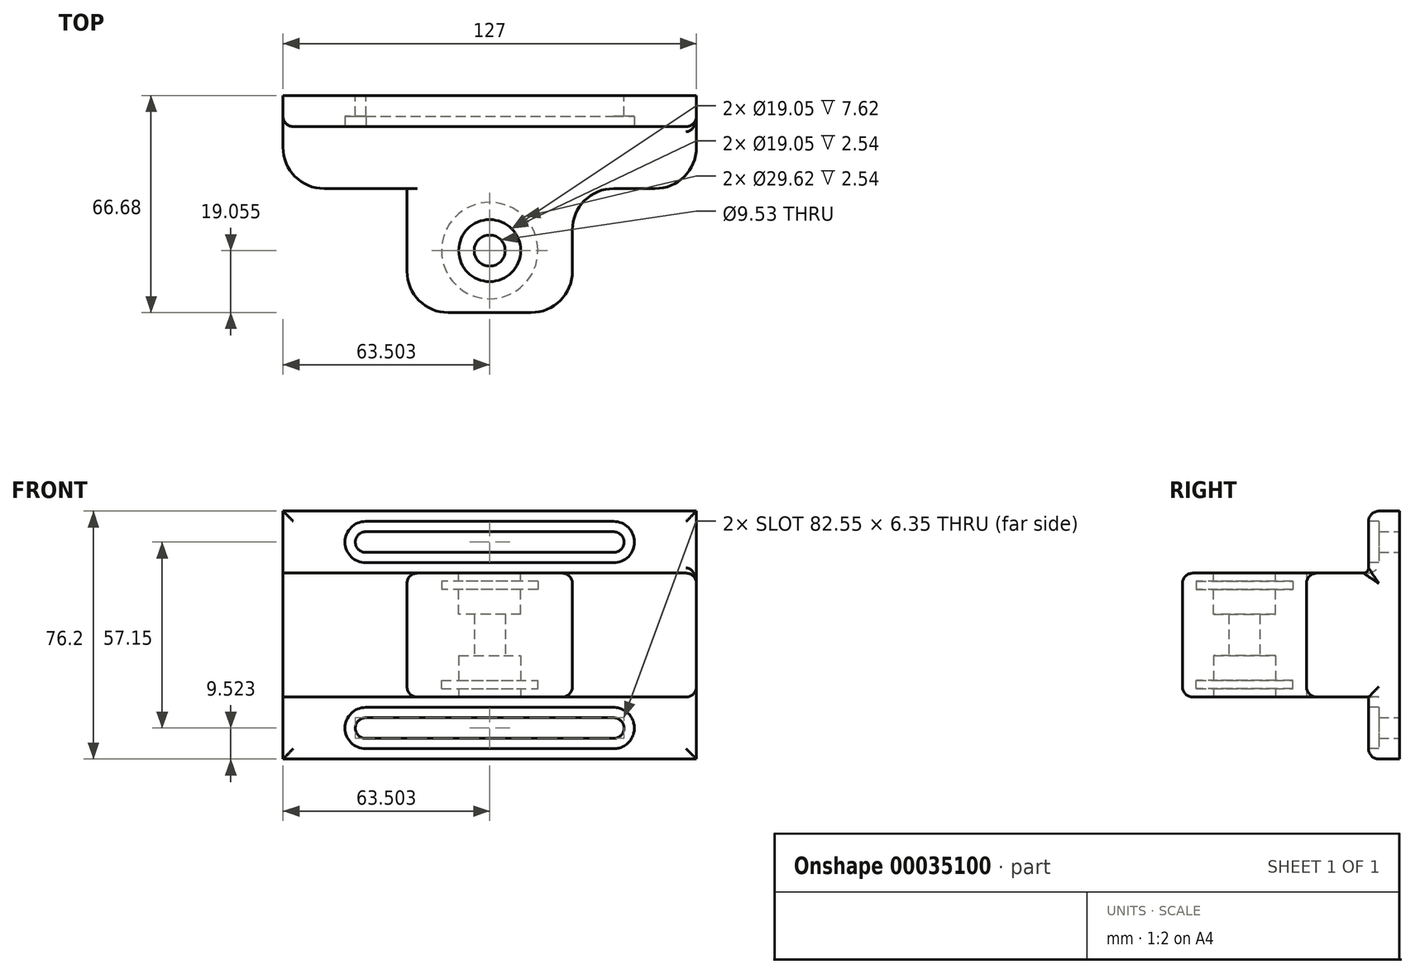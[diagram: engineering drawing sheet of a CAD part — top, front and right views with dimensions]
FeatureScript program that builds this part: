
annotation { "Feature Type Name" : "Feature", "Feature Type Description" : "" }
export const myFeature = defineFeature(function(context is Context, id is Id, definition is map)
    precondition{}
    {
        {
            var Q0;
            Q0=qCreatedBy(makeId("Front.planeOp"),FACE);
            var sketch = newSketch(context, id + "F0", { "sketchPlane" : qUnion([Q0])});
            skLineSegment(sketch, "E0.bottom", {"start": v(-64.26, 39.5) * mm, "end": v(62.74, 39.5) * mm});
            skLineSegment(sketch, "E0.top", {"start": v(-64.26, -36.7) * mm, "end": v(62.74, -36.7) * mm});
            skLineSegment(sketch, "E0.left", {"start": v(-64.26, 39.5) * mm, "end": v(-64.26, -36.7) * mm});
            skLineSegment(sketch, "E0.right", {"start": v(62.74, 39.5) * mm, "end": v(62.74, -36.7) * mm});
            skArc(sketch, "E1", {"start": v(-38.86, -24) * mm, "mid": v(-42.03, -27.23) * mm, "end": v(-38.74, -30.35) * mm});
            skArc(sketch, "E2", {"start": v(37.34, -30.35) * mm, "mid": v(40.52, -27.18) * mm, "end": v(37.34, -24) * mm});
            skLineSegment(sketch, "E3", {"start": v(-38.86, -24) * mm, "end": v(37.34, -24) * mm});
            skLineSegment(sketch, "E4", {"start": v(-38.97, -30.35) * mm, "end": v(37.34, -30.35) * mm});
            skLineSegment(sketch, "E5", {"start": v(-64.26, 1.4) * mm, "end": v(62.74, 1.4) * mm, "construction": true});
            skLineSegment(sketch, "E6.MirrorCS", {"start": v(-38.86, 26.8) * mm, "end": v(37.34, 26.8) * mm});
            skLineSegment(sketch, "E7.MirrorCS", {"start": v(-38.97, 33.15) * mm, "end": v(37.34, 33.15) * mm});
            skArc(sketch, "E8.MirrorCS", {"start": v(-38.86, 26.8) * mm, "mid": v(-42.03, 30.03) * mm, "end": v(-38.74, 33.15) * mm});
            skArc(sketch, "E9.MirrorCS", {"start": v(37.34, 33.15) * mm, "mid": v(40.52, 29.97) * mm, "end": v(37.34, 26.8) * mm});
            skSolve(sketch);
        }
        {
            var Q0;
            Q0 = qSketchRegion(id + "F0", true);
            extrude(context, id + "F1", {"entities" : qUnion([Q0]), "depth" : 9.52 * mm});
        }
        {
            var Q0;
            Q0=makeQuery(id+"F1.opExtrude","CAP_FACE",FACE,{"disambiguationData":[OSD([sQuery(id+"F0.wireOp",EDGE,"E0.bottom"),sQuery(id+"F0.wireOp",EDGE,"E0.top"),sQuery(id+"F0.wireOp",EDGE,"E0.left"),sQuery(id+"F0.wireOp",EDGE,"E0.right"),sQuery(id+"F0.wireOp",EDGE,"E1"),sQuery(id+"F0.wireOp",EDGE,"E2"),sQuery(id+"F0.wireOp",EDGE,"E3"),sQuery(id+"F0.wireOp",EDGE,"E4"),sQuery(id+"F0.wireOp",EDGE,"E6.MirrorCS"),sQuery(id+"F0.wireOp",EDGE,"E7.MirrorCS"),sQuery(id+"F0.wireOp",EDGE,"E8.MirrorCS"),sQuery(id+"F0.wireOp",EDGE,"E9.MirrorCS")])],"isStart":false});
            var sketch = newSketch(context, id + "F2", { "sketchPlane" : qUnion([Q0])});
            skArc(sketch, "E10", {"start": v(-38.86, -20.83) * mm, "mid": v(-45.2, -27.23) * mm, "end": v(-38.75, -33.53) * mm});
            skArc(sketch, "E11", {"start": v(37.34, -33.53) * mm, "mid": v(43.7, -27.18) * mm, "end": v(37.34, -20.83) * mm});
            skLineSegment(sketch, "E12", {"start": v(-38.86, -20.83) * mm, "end": v(37.34, -20.83) * mm});
            skLineSegment(sketch, "E13", {"start": v(-38.75, -33.53) * mm, "end": v(37.34, -33.53) * mm});
            skLineSegment(sketch, "E14", {"start": v(-64.26, 1.4) * mm, "end": v(62.74, 1.4) * mm, "construction": true});
            skLineSegment(sketch, "E15.MirrorCS", {"start": v(-38.86, 23.62) * mm, "end": v(37.34, 23.62) * mm});
            skLineSegment(sketch, "E16.MirrorCS", {"start": v(-38.75, 36.32) * mm, "end": v(37.34, 36.32) * mm});
            skArc(sketch, "E17.MirrorCS", {"start": v(-38.86, 23.62) * mm, "mid": v(-45.2, 30.03) * mm, "end": v(-38.75, 36.32) * mm});
            skArc(sketch, "E18.MirrorCS", {"start": v(37.34, 36.32) * mm, "mid": v(43.7, 29.97) * mm, "end": v(37.34, 23.62) * mm});
            skSolve(sketch);
        }
        {
            var Q0;
            Q0=makeQuery(id+"F2.imprint","IMPRINT",FACE,{"disambiguationData":[TD([[makeQuery(id+"F2.imprint","IMPRINT",EDGE,{"derivedFrom":sQuery(id+"F2.wireOp",EDGE,"E15.MirrorCS")}),1.0]])]});
            var Q1;
            Q1=makeQuery(id+"F2.imprint","IMPRINT",FACE,{"disambiguationData":[TD([[makeQuery(id+"F2.imprint","IMPRINT",EDGE,{"derivedFrom":sQuery(id+"F2.wireOp",EDGE,"E10")}),1.0]])]});
            extrude(context, id + "F3", {"entities" : qUnion([Q0, Q1]), "operationType" : NewBodyOperationType.REMOVE, "oppositeDirection" : true, "depth" : 3.17 * mm});
        }
        {
            var Q0;
            Q0=makeQuery(id+"F1.opExtrude","CAP_FACE",FACE,{"disambiguationData":[OSD([sQuery(id+"F0.wireOp",EDGE,"E0.bottom"),sQuery(id+"F0.wireOp",EDGE,"E0.top"),sQuery(id+"F0.wireOp",EDGE,"E0.left"),sQuery(id+"F0.wireOp",EDGE,"E0.right"),sQuery(id+"F0.wireOp",EDGE,"E1"),sQuery(id+"F0.wireOp",EDGE,"E2"),sQuery(id+"F0.wireOp",EDGE,"E3"),sQuery(id+"F0.wireOp",EDGE,"E4"),sQuery(id+"F0.wireOp",EDGE,"E6.MirrorCS"),sQuery(id+"F0.wireOp",EDGE,"E7.MirrorCS"),sQuery(id+"F0.wireOp",EDGE,"E8.MirrorCS"),sQuery(id+"F0.wireOp",EDGE,"E9.MirrorCS")])],"isStart":false});
            var sketch = newSketch(context, id + "F4", { "sketchPlane" : qUnion([Q0])});
            skLineSegment(sketch, "E19.bottom", {"start": v(-64.26, -17.65) * mm, "end": v(62.74, -17.65) * mm});
            skLineSegment(sketch, "E19.top", {"start": v(-64.26, 20.45) * mm, "end": v(62.74, 20.45) * mm});
            skLineSegment(sketch, "E19.left", {"start": v(-64.26, -17.65) * mm, "end": v(-64.26, 20.45) * mm});
            skLineSegment(sketch, "E19.right", {"start": v(62.74, -17.65) * mm, "end": v(62.74, 20.45) * mm});
            skSolve(sketch);
        }
        {
            var Q0;
            Q0=makeQuery(id+"F4.imprint","IMPRINT",FACE,{"disambiguationData":[TD([[makeQuery(id+"F4.imprint","IMPRINT",EDGE,{"derivedFrom":sQuery(id+"F4.wireOp",EDGE,"E19.bottom")}),1.0]])]});
            extrude(context, id + "F5", {"entities" : qUnion([Q0]), "operationType" : NewBodyOperationType.ADD, "depth" : 19.05 * mm});
        }
        {
            var Q0;
            Q0=makeQuery(id+"F5.opExtrude","CAP_FACE",FACE,{"disambiguationData":[OSD([sQuery(id+"F4.wireOp",EDGE,"E19.bottom"),sQuery(id+"F4.wireOp",EDGE,"E19.top"),sQuery(id+"F4.wireOp",EDGE,"E19.left"),sQuery(id+"F4.wireOp",EDGE,"E19.right")])],"isStart":false});
            var sketch = newSketch(context, id + "F6", { "sketchPlane" : qUnion([Q0])});
            skLineSegment(sketch, "E20.bottom", {"start": v(-26.16, 20.45) * mm, "end": v(24.64, 20.45) * mm});
            skLineSegment(sketch, "E20.top", {"start": v(-26.16, -17.65) * mm, "end": v(24.64, -17.65) * mm});
            skLineSegment(sketch, "E20.left", {"start": v(-26.16, 20.45) * mm, "end": v(-26.16, -17.65) * mm});
            skLineSegment(sketch, "E20.right", {"start": v(24.64, 20.45) * mm, "end": v(24.64, -17.65) * mm});
            skSolve(sketch);
        }
        {
            var Q0;
            Q0=makeQuery(id+"F6.imprint","IMPRINT",FACE,{"disambiguationData":[TD([[makeQuery(id+"F6.imprint","IMPRINT",EDGE,{"derivedFrom":sQuery(id+"F6.wireOp",EDGE,"E20.bottom")}),-1.0]])]});
            extrude(context, id + "F7", {"entities" : qUnion([Q0]), "operationType" : NewBodyOperationType.ADD, "depth" : 38.1 * mm});
        }
        {
            var Q0;
            Q0=makeQuery(id+"F7.boolean.opBoolean","MERGE",FACE,{"derivedFrom":[makeQuery(id+"F5.opExtrude","SWEPT_FACE",FACE,{"disambiguationData":[OSD([sQuery(id+"F4.wireOp",EDGE,"E19.bottom")])]}),makeQuery(id+"F7.opExtrude","SWEPT_FACE",FACE,{"disambiguationData":[OSD([sQuery(id+"F6.wireOp",EDGE,"E20.top")])]})]});
            var sketch = newSketch(context, id + "F8", { "sketchPlane" : qUnion([Q0])});
            skPoint(sketch, "E21", {"position": v(-0.76, 47.63) * mm});
            skSolve(sketch);
        }
        {
            var Q0;
            Q0=sQuery(id+"F8.wireOp",VERTEX,"E21");
            var Q1;
            Q1=makeQuery(id+"F1.opExtrude","SWEPT_BODY",BODY,{"disambiguationData":[OSD([sQuery(id+"F0.wireOp",EDGE,"E0.bottom"),sQuery(id+"F0.wireOp",EDGE,"E0.top"),sQuery(id+"F0.wireOp",EDGE,"E0.left"),sQuery(id+"F0.wireOp",EDGE,"E0.right"),sQuery(id+"F0.wireOp",EDGE,"E1"),sQuery(id+"F0.wireOp",EDGE,"E2"),sQuery(id+"F0.wireOp",EDGE,"E3"),sQuery(id+"F0.wireOp",EDGE,"E4"),sQuery(id+"F0.wireOp",EDGE,"E6.MirrorCS"),sQuery(id+"F0.wireOp",EDGE,"E7.MirrorCS"),sQuery(id+"F0.wireOp",EDGE,"E8.MirrorCS"),sQuery(id+"F0.wireOp",EDGE,"E9.MirrorCS")])]});
            hole(context, id + "F9", {"style" : HoleStyle.C_BORE, "holeDiameter" : 9.52 * mm, "cBoreDiameter" : 19.05 * mm, "cBoreDepth" : 12.7 * mm, "endStyle" : HoleEndStyle.THROUGH, "locations" : qUnion([Q0]), "scope" : qUnion([Q1])});
        }
        {
            var Q0;
            Q0=makeQuery(id+"F7.boolean.opBoolean","MERGE",FACE,{"derivedFrom":[makeQuery(id+"F5.opExtrude","SWEPT_FACE",FACE,{"disambiguationData":[OSD([sQuery(id+"F4.wireOp",EDGE,"E19.top")])]}),makeQuery(id+"F7.opExtrude","SWEPT_FACE",FACE,{"disambiguationData":[OSD([sQuery(id+"F6.wireOp",EDGE,"E20.bottom")])]})]});
            var sketch = newSketch(context, id + "F10", { "sketchPlane" : qUnion([Q0])});
            skCircle(sketch, "E22.0.0", {"center": v(-0.76, -47.63) * mm, "radius": 9.52 * mm});
            skSolve(sketch);
        }
        {
            var Q0;
            Q0=makeQuery(id+"F10.imprint","IMPRINT",FACE,{"disambiguationData":[TD([[makeQuery(id+"F10.imprint","IMPRINT",EDGE,{"derivedFrom":sQuery(id+"F10.wireOp",EDGE,"E22.0.0")}),1.0]])]});
            extrude(context, id + "F11", {"entities" : qUnion([Q0]), "operationType" : NewBodyOperationType.REMOVE, "oppositeDirection" : true, "depth" : 12.7 * mm});
        }
        {
            var Q0;
            Q0=makeQuery(id+"F7.opExtrude","CAP_EDGE",EDGE,{"disambiguationData":[OSD([sQuery(id+"F6.wireOp",EDGE,"E20.right")])],"isStart":false});
            var Q1;
            Q1=makeQuery(id+"F7.opExtrude","CAP_EDGE",EDGE,{"disambiguationData":[OSD([sQuery(id+"F6.wireOp",EDGE,"E20.left")])],"isStart":false});
            var Q2;
            Q2=makeQuery(id+"F7.opExtrude","CAP_EDGE",EDGE,{"disambiguationData":[OSD([sQuery(id+"F6.wireOp",EDGE,"E20.right")])],"isStart":true});
            var Q3;
            Q3=makeQuery(id+"F5.opExtrude","CAP_EDGE",EDGE,{"disambiguationData":[OSD([sQuery(id+"F4.wireOp",EDGE,"E19.right")])],"isStart":false});
            var Q4;
            Q4=makeQuery(id+"F7.opExtrude","CAP_EDGE",EDGE,{"disambiguationData":[OSD([sQuery(id+"F6.wireOp",EDGE,"E20.left")])],"isStart":true});
            var Q5;
            Q5=makeQuery(id+"F5.opExtrude","CAP_EDGE",EDGE,{"disambiguationData":[OSD([sQuery(id+"F4.wireOp",EDGE,"E19.left")])],"isStart":false});
            fillet(context, id + "F12", {"entities" : qUnion([Q0, Q1, Q2, Q3, Q4, Q5]), "radius" : 12.7 * mm, "tangentPropagation" : true, "allowEdgeOverflow" : false});
        }
        {
            var Q0;
            Q0=makeQuery(id+"F1.opExtrude","CAP_EDGE",EDGE,{"disambiguationData":[OSD([sQuery(id+"F0.wireOp",EDGE,"E0.top")])],"isStart":false});
            var Q1;
            Q1=makeQuery(id+"F5.opExtrude","SWEPT_EDGE",EDGE,{"disambiguationData":[OSD([sQuery(id+"F0.wireOp",EDGE,"E0.right"),sQuery(id+"F4.wireOp",EDGE,"E19.bottom"),sQuery(id+"F4.wireOp",EDGE,"E19.right")])]});
            var Q2;
            Q2=makeQuery(id+"F12.opFillet","BLEND_EDGE",EDGE,{"blendedFrom":[makeQuery(id+"F5.opExtrude","CAP_EDGE",EDGE,{"disambiguationData":[OSD([sQuery(id+"F4.wireOp",EDGE,"E19.right")])],"isStart":false}),makeQuery(id+"F7.boolean.opBoolean","MERGE",FACE,{"derivedFrom":[makeQuery(id+"F5.opExtrude","SWEPT_FACE",FACE,{"disambiguationData":[OSD([sQuery(id+"F4.wireOp",EDGE,"E19.bottom")])]}),makeQuery(id+"F7.opExtrude","SWEPT_FACE",FACE,{"disambiguationData":[OSD([sQuery(id+"F6.wireOp",EDGE,"E20.top")])]})]})],"blendedInto":[makeQuery(id+"F7.boolean.opBoolean","MERGE",FACE,{"derivedFrom":[makeQuery(id+"F5.opExtrude","SWEPT_FACE",FACE,{"disambiguationData":[OSD([sQuery(id+"F4.wireOp",EDGE,"E19.bottom")])]}),makeQuery(id+"F7.opExtrude","SWEPT_FACE",FACE,{"disambiguationData":[OSD([sQuery(id+"F6.wireOp",EDGE,"E20.top")])]})]})]});
            var Q3;
            Q3=makeQuery(id+"F5.opExtrude","SWEPT_EDGE",EDGE,{"disambiguationData":[OSD([sQuery(id+"F0.wireOp",EDGE,"E0.right"),sQuery(id+"F4.wireOp",EDGE,"E19.top"),sQuery(id+"F4.wireOp",EDGE,"E19.right")])]});
            var Q4;
            Q4=makeQuery(id+"F1.opExtrude","CAP_EDGE",EDGE,{"disambiguationData":[OSD([sQuery(id+"F0.wireOp",EDGE,"E0.bottom")])],"isStart":false});
            var Q5;
            {var subQ0=sQuery(id+"F0.wireOp",EDGE,"E0.right");var subQ1=sQuery(id+"F0.wireOp",EDGE,"E0.bottom");Q5=makeQuery(id+"F5.boolean.opBoolean","SPLIT",EDGE,{"disambiguationData":[TD([makeQuery(id+"F1.opExtrude","SWEPT_FACE",FACE,{"disambiguationData":[OSD([subQ1])]})])],"derivedFrom":makeQuery(id+"F1.opExtrude","CAP_EDGE",EDGE,{"disambiguationData":[OSD([subQ0])],"isStart":false})});}
            var Q6;
            {var subQ0=sQuery(id+"F0.wireOp",EDGE,"E0.right");var subQ1=sQuery(id+"F0.wireOp",EDGE,"E0.top");Q6=makeQuery(id+"F5.boolean.opBoolean","SPLIT",EDGE,{"disambiguationData":[TD([makeQuery(id+"F1.opExtrude","SWEPT_FACE",FACE,{"disambiguationData":[OSD([subQ1])]})])],"derivedFrom":makeQuery(id+"F1.opExtrude","CAP_EDGE",EDGE,{"disambiguationData":[OSD([subQ0])],"isStart":false})});}
            var Q7;
            {var subQ0=sQuery(id+"F0.wireOp",EDGE,"E0.left");var subQ1=sQuery(id+"F0.wireOp",EDGE,"E0.top");Q7=makeQuery(id+"F5.boolean.opBoolean","SPLIT",EDGE,{"disambiguationData":[TD([makeQuery(id+"F1.opExtrude","SWEPT_FACE",FACE,{"disambiguationData":[OSD([subQ1])]})])],"derivedFrom":makeQuery(id+"F1.opExtrude","CAP_EDGE",EDGE,{"disambiguationData":[OSD([subQ0])],"isStart":false})});}
            var Q8;
            {var subQ0=sQuery(id+"F0.wireOp",EDGE,"E0.left");var subQ1=sQuery(id+"F0.wireOp",EDGE,"E0.bottom");Q8=makeQuery(id+"F5.boolean.opBoolean","SPLIT",EDGE,{"disambiguationData":[TD([makeQuery(id+"F1.opExtrude","SWEPT_FACE",FACE,{"disambiguationData":[OSD([subQ1])]})])],"derivedFrom":makeQuery(id+"F1.opExtrude","CAP_EDGE",EDGE,{"disambiguationData":[OSD([subQ0])],"isStart":false})});}
            fillet(context, id + "F13", {"entities" : qUnion([Q0, Q1, Q2, Q3, Q4, Q5, Q6, Q7, Q8]), "radius" : 3.17 * mm, "tangentPropagation" : true, "allowEdgeOverflow" : false});
        }
        {
            var Q0;
            Q0=makeQuery(id+"F1.opExtrude","SWEPT_FACE",FACE,{"disambiguationData":[OSD([sQuery(id+"F0.wireOp",EDGE,"E0.top")])]});
            cPlane(context, id + "F14", {"entities" : qUnion([Q0]), "cplaneType" : CPlaneType.OFFSET, "offset" : 24.13 * mm, "oppositeDirection" : true, "width" : 152.4 * mm, "height" : 152.4 * mm});
        }
        {
            var Q0;
            Q0=qCreatedBy(id+"F14.planeOp",FACE);
            var sketch = newSketch(context, id + "F15", { "sketchPlane" : qUnion([Q0])});
            skCircle(sketch, "E23", {"center": v(-0.76, 47.63) * mm, "radius": 14.8 * mm});
            skSolve(sketch);
        }
        {
            var Q0;
            Q0=makeQuery(id+"F1.opExtrude","SWEPT_FACE",FACE,{"disambiguationData":[OSD([sQuery(id+"F0.wireOp",EDGE,"E0.bottom")])]});
            cPlane(context, id + "F16", {"entities" : qUnion([Q0]), "cplaneType" : CPlaneType.OFFSET, "offset" : 24.13 * mm, "oppositeDirection" : true, "width" : 152.4 * mm, "height" : 152.4 * mm});
        }
        {
            var Q0;
            Q0=qCreatedBy(id+"F16.planeOp",FACE);
            var sketch = newSketch(context, id + "F17", { "sketchPlane" : qUnion([Q0])});
            skCircle(sketch, "E24.0", {"center": v(-0.76, -47.63) * mm, "radius": 14.8 * mm});
            skSolve(sketch);
        }
        {
            var Q0;
            Q0 = qSketchRegion(id + "F17", true);
            var Q1;
            Q1=makeQuery(id+"F7.boolean.opBoolean","MERGE",FACE,{"derivedFrom":[makeQuery(id+"F5.opExtrude","SWEPT_FACE",FACE,{"disambiguationData":[OSD([sQuery(id+"F4.wireOp",EDGE,"E19.top")])]}),makeQuery(id+"F7.opExtrude","SWEPT_FACE",FACE,{"disambiguationData":[OSD([sQuery(id+"F6.wireOp",EDGE,"E20.bottom")])]})]});
            extrude(context, id + "F18", {"entities" : qUnion([Q0, Q1]), "operationType" : NewBodyOperationType.REMOVE, "depth" : 2.54 * mm});
        }
        {
            var Q0;
            Q0 = qSketchRegion(id + "F15", true);
            var Q1;
            Q1=makeQuery(id+"F7.boolean.opBoolean","MERGE",FACE,{"derivedFrom":[makeQuery(id+"F5.opExtrude","SWEPT_FACE",FACE,{"disambiguationData":[OSD([sQuery(id+"F4.wireOp",EDGE,"E19.bottom")])]}),makeQuery(id+"F7.opExtrude","SWEPT_FACE",FACE,{"disambiguationData":[OSD([sQuery(id+"F6.wireOp",EDGE,"E20.top")])]})]});
            extrude(context, id + "F19", {"entities" : qUnion([Q0, Q1]), "operationType" : NewBodyOperationType.REMOVE, "depth" : 2.54 * mm});
        }
        {
            var Q0;
            Q0=makeQuery(id+"F5.opExtrude","CAP_EDGE",EDGE,{"disambiguationData":[OSD([sQuery(id+"F4.wireOp",EDGE,"E19.top")])],"isStart":true});
            var Q1;
            Q1=makeQuery(id+"F5.opExtrude","CAP_EDGE",EDGE,{"disambiguationData":[OSD([sQuery(id+"F4.wireOp",EDGE,"E19.bottom")])],"isStart":true});
            fillet(context, id + "F20", {"entities" : qUnion([Q0, Q1]), "radius" : 1.59 * mm, "tangentPropagation" : true, "allowEdgeOverflow" : false});
        }
    });
